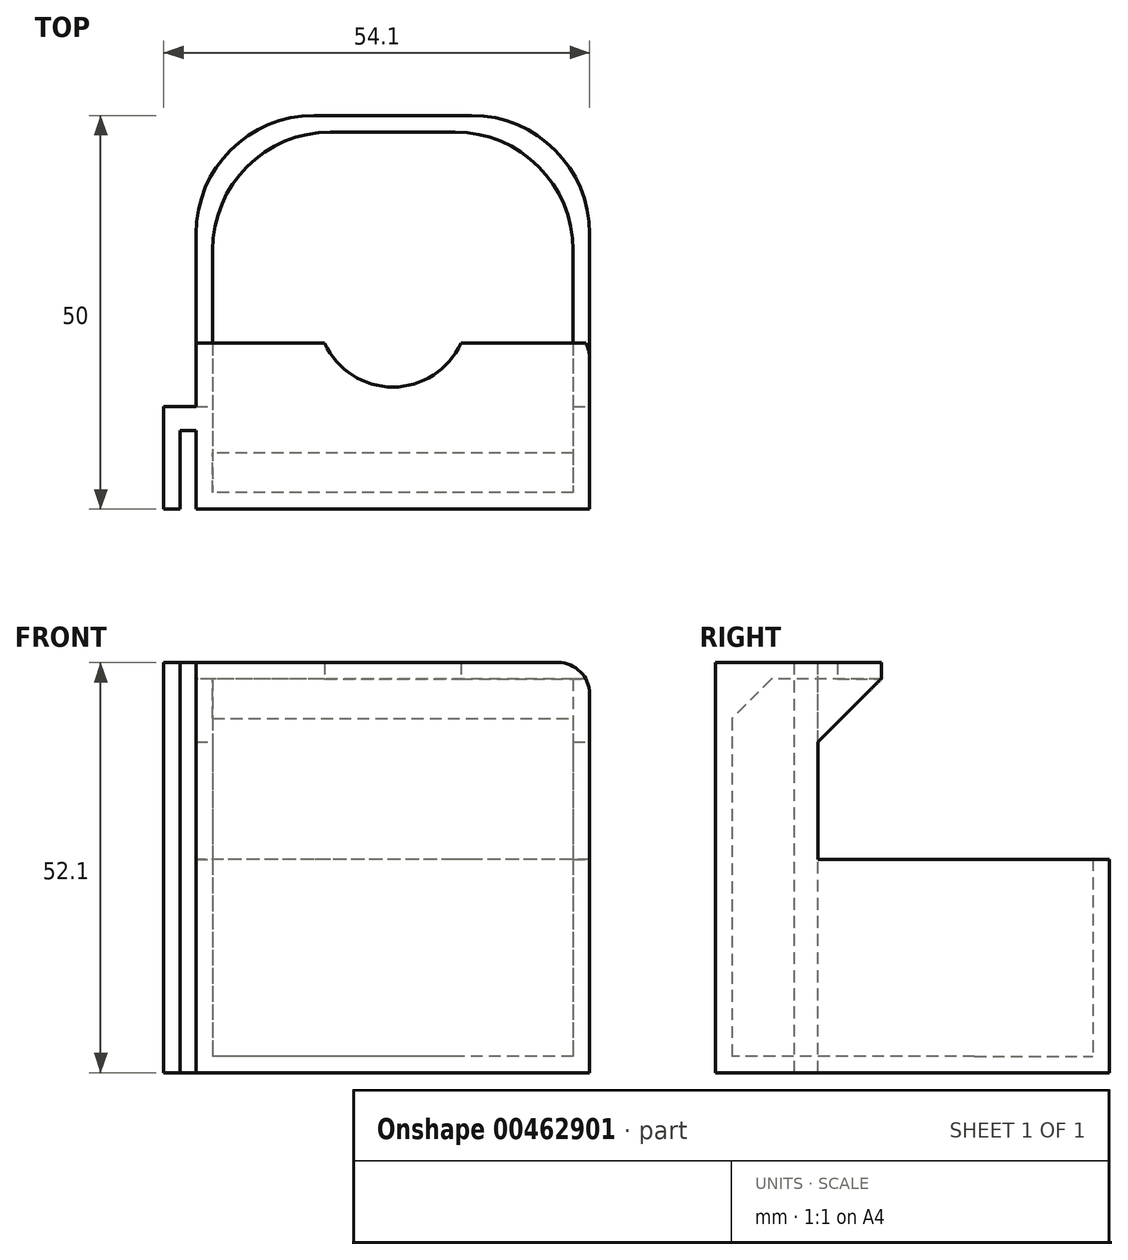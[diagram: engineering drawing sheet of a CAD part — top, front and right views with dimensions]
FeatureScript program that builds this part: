
annotation { "Feature Type Name" : "Feature", "Feature Type Description" : "" }
export const myFeature = defineFeature(function(context is Context, id is Id, definition is map)
    precondition{}
    {
        {
            var Q0;
            Q0=qCreatedBy(makeId("Top.planeOp"),FACE);
            var sketch = newSketch(context, id + "F0", { "sketchPlane" : qUnion([Q0])});
            skLineSegment(sketch, "E0.bottom", {"start": v(25, -25) * mm, "end": v(-25, -25) * mm});
            skLineSegment(sketch, "E0.top", {"start": v(10, 25) * mm, "end": v(-10, 25) * mm});
            skLineSegment(sketch, "E0.left", {"start": v(25, -25) * mm, "end": v(25, 10) * mm});
            skLineSegment(sketch, "E0.right", {"start": v(-25, -25) * mm, "end": v(-25, -15) * mm});
            skPoint(sketch, "E0.middle", {"position": v(0, 0) * mm});
            skLineSegment(sketch, "E1", {"start": v(-25, -25) * mm, "end": v(-27, -25) * mm, "construction": true});
            skLineSegment(sketch, "E2", {"start": v(-27, -25) * mm, "end": v(-27, -15) * mm});
            skLineSegment(sketch, "E3", {"start": v(-27, -25) * mm, "end": v(-29.1, -25) * mm});
            skLineSegment(sketch, "E4", {"start": v(-29.1, -25) * mm, "end": v(-29.1, -12) * mm});
            skLineSegment(sketch, "E5", {"start": v(-29.1, -12) * mm, "end": v(-25, -12) * mm});
            skLineSegment(sketch, "E6", {"start": v(-27, -15) * mm, "end": v(-25, -15) * mm});
            skLineSegment(sketch, "E7.trimOffspring", {"start": v(-25, -12) * mm, "end": v(-25, 10) * mm});
            skLineSegment(sketch, "E8.bottom", {"start": v(7.9, 22.9) * mm, "end": v(-7.9, 22.9) * mm});
            skLineSegment(sketch, "E8.top", {"start": v(22.9, -22.9) * mm, "end": v(-22.9, -22.9) * mm});
            skLineSegment(sketch, "E8.left", {"start": v(22.9, 7.9) * mm, "end": v(22.9, -22.9) * mm});
            skLineSegment(sketch, "E8.right", {"start": v(-22.9, 7.9) * mm, "end": v(-22.9, -22.9) * mm});
            skPoint(sketch, "E9.visualSharp", {"position": v(22.9, 22.9) * mm});
            skArc(sketch, "E9.filletArc", {"start": v(22.9, 7.9) * mm, "mid": v(18.5, 18.5) * mm, "end": v(7.9, 22.9) * mm});
            skPoint(sketch, "E10.visualSharp", {"position": v(-22.9, 22.9) * mm});
            skArc(sketch, "E10.filletArc", {"start": v(-7.9, 22.9) * mm, "mid": v(-18.5, 18.5) * mm, "end": v(-22.9, 7.9) * mm});
            skPoint(sketch, "E11.visualSharp", {"position": v(-25, 25) * mm});
            skArc(sketch, "E11.filletArc", {"start": v(-10, 25) * mm, "mid": v(-20.6, 20.6) * mm, "end": v(-25, 10) * mm});
            skPoint(sketch, "E12.visualSharp", {"position": v(25, 25) * mm});
            skArc(sketch, "E12.filletArc", {"start": v(25, 10) * mm, "mid": v(20.6, 20.6) * mm, "end": v(10, 25) * mm});
            skCircle(sketch, "E13", {"center": v(0, 0) * mm, "radius": 9.5 * mm});
            skLineSegment(sketch, "E14", {"start": v(-8.64, -3.94) * mm, "end": v(-22.9, -3.94) * mm});
            skLineSegment(sketch, "E15", {"start": v(-22.9, -3.94) * mm, "end": v(22.9, -3.94) * mm});
            skLineSegment(sketch, "E16", {"start": v(-22.9, -22.9) * mm, "end": v(-25, -22.9) * mm});
            skLineSegment(sketch, "E17", {"start": v(22.9, -22.9) * mm, "end": v(25, -22.9) * mm});
            skLineSegment(sketch, "E18", {"start": v(-25, -12) * mm, "end": v(-22.9, -12) * mm});
            skLineSegment(sketch, "E19", {"start": v(22.9, -12) * mm, "end": v(25, -12) * mm});
            skLineSegment(sketch, "E20", {"start": v(-25, -3.94) * mm, "end": v(25, -3.94) * mm});
            skSolve(sketch);
        }
        {
            var Q0;
            Q0=makeQuery(id+"F0.imprint","IMPRINT",FACE,{"disambiguationData":[TD([[makeQuery(id+"F0.imprint","IMPRINT",EDGE,{"derivedFrom":sQuery(id+"F0.wireOp",EDGE,"E8.bottom")}),1.0]])]});
            var Q1;
            {var subQ1=sQuery(id+"F0.wireOp",EDGE,"E8.top");Q1=makeQuery(id+"F0.imprint","IMPRINT",FACE,{"disambiguationData":[TD([[makeQuery(id+"F0.imprint","IMPRINT",EDGE,{"derivedFrom":subQ1}),-1.0]])]});}
            var Q2;
            {var subQ0=sQuery(id+"F0.wireOp",EDGE,"E15");var subQ1=sQuery(id+"F0.wireOp",EDGE,"E13");var subQ2=makeQuery(id+"F0.imprint","INTERSECT",VERTEX,{"disambiguationData":[OD(0.0)],"derivedFrom":[subQ1,subQ0]});Q2=makeQuery(id+"F0.imprint","IMPRINT",FACE,{"disambiguationData":[TD([[makeQuery(id+"F0.imprint","IMPRINT",EDGE,{"disambiguationData":[TD([[subQ2,1.0]])],"derivedFrom":subQ1}),1.0]])]});}
            var Q3;
            Q3=makeQuery(id+"F0.imprint","IMPRINT",FACE,{"disambiguationData":[TD([[makeQuery(id+"F0.imprint","IMPRINT",EDGE,{"derivedFrom":sQuery(id+"F0.wireOp",EDGE,"E0.top")}),1.0]])]});
            var Q4;
            {var subQ0=sQuery(id+"F0.wireOp",EDGE,"E15");var subQ1=sQuery(id+"F0.wireOp",EDGE,"E13");var subQ2=makeQuery(id+"F0.imprint","INTERSECT",VERTEX,{"disambiguationData":[OD(0.0)],"derivedFrom":[subQ1,subQ0]});Q4=makeQuery(id+"F0.imprint","IMPRINT",FACE,{"disambiguationData":[TD([[makeQuery(id+"F0.imprint","IMPRINT",EDGE,{"disambiguationData":[TD([[subQ2,-1.0]])],"derivedFrom":subQ1}),1.0]])]});}
            var Q5;
            Q5=makeQuery(id+"F0.imprint","IMPRINT",FACE,{"disambiguationData":[TD([[makeQuery(id+"F0.imprint","IMPRINT",EDGE,{"derivedFrom":sQuery(id+"F0.wireOp",EDGE,"E2")}),1.0]])]});
            var Q6;
            {var subQ1=sQuery(id+"F0.wireOp",EDGE,"E0.bottom");Q6=makeQuery(id+"F0.imprint","IMPRINT",FACE,{"disambiguationData":[TD([[makeQuery(id+"F0.imprint","IMPRINT",EDGE,{"derivedFrom":subQ1}),-1.0]])]});}
            var Q7;
            {var subQ0=sQuery(id+"F0.wireOp",EDGE,"E18");Q7=makeQuery(id+"F0.imprint","IMPRINT",FACE,{"disambiguationData":[TD([[makeQuery(id+"F0.imprint","IMPRINT",EDGE,{"derivedFrom":subQ0}),1.0]])]});}
            var Q8;
            {var subQ0=sQuery(id+"F0.wireOp",EDGE,"E19");Q8=makeQuery(id+"F0.imprint","IMPRINT",FACE,{"disambiguationData":[TD([[makeQuery(id+"F0.imprint","IMPRINT",EDGE,{"derivedFrom":subQ0}),1.0]])]});}
            var Q9;
            {var subQ0=sQuery(id+"F0.wireOp",EDGE,"E17");Q9=makeQuery(id+"F0.imprint","IMPRINT",FACE,{"disambiguationData":[TD([[makeQuery(id+"F0.imprint","IMPRINT",EDGE,{"derivedFrom":subQ0}),1.0]])]});}
            extrude(context, id + "F1", {"entities" : qUnion([Q0, Q1, Q2, Q3, Q4, Q5, Q6, Q7, Q8, Q9]), "oppositeDirection" : true, "depth" : 2.1 * mm});
        }
        {
            var Q0;
            {var subQ5=sQuery(id+"F0.wireOp",EDGE,"E8.top");Q0=makeQuery(id+"F0.imprint","IMPRINT",FACE,{"disambiguationData":[TD([[makeQuery(id+"F0.imprint","IMPRINT",EDGE,{"derivedFrom":subQ5}),-1.0]])]});}
            var Q1;
            Q1=makeQuery(id+"F0.imprint","IMPRINT",FACE,{"disambiguationData":[TD([[makeQuery(id+"F0.imprint","IMPRINT",EDGE,{"derivedFrom":sQuery(id+"F0.wireOp",EDGE,"E2")}),1.0]])]});
            var Q2;
            {var subQ1=sQuery(id+"F0.wireOp",EDGE,"E0.bottom");Q2=makeQuery(id+"F0.imprint","IMPRINT",FACE,{"disambiguationData":[TD([[makeQuery(id+"F0.imprint","IMPRINT",EDGE,{"derivedFrom":subQ1}),-1.0]])]});}
            var Q3;
            {var subQ0=sQuery(id+"F0.wireOp",EDGE,"E17");Q3=makeQuery(id+"F0.imprint","IMPRINT",FACE,{"disambiguationData":[TD([[makeQuery(id+"F0.imprint","IMPRINT",EDGE,{"derivedFrom":subQ0}),1.0]])]});}
            var Q4;
            {var subQ0=sQuery(id+"F0.wireOp",EDGE,"E18");Q4=makeQuery(id+"F0.imprint","IMPRINT",FACE,{"disambiguationData":[TD([[makeQuery(id+"F0.imprint","IMPRINT",EDGE,{"derivedFrom":subQ0}),1.0]])]});}
            var Q5;
            {var subQ0=sQuery(id+"F0.wireOp",EDGE,"E19");Q5=makeQuery(id+"F0.imprint","IMPRINT",FACE,{"disambiguationData":[TD([[makeQuery(id+"F0.imprint","IMPRINT",EDGE,{"derivedFrom":subQ0}),1.0]])]});}
            extrude(context, id + "F2", {"entities" : qUnion([Q0, Q1, Q2, Q3, Q4, Q5]), "operationType" : NewBodyOperationType.ADD, "depth" : 50 * mm, "hasSecondDirection" : true, "secondDirectionOppositeDirection" : true, "secondDirectionDepth" : 2.1 * mm});
        }
        {
            var Q0;
            {var subQ5=sQuery(id+"F0.wireOp",EDGE,"E8.top");Q0=makeQuery(id+"F0.imprint","IMPRINT",FACE,{"disambiguationData":[TD([[makeQuery(id+"F0.imprint","IMPRINT",EDGE,{"derivedFrom":subQ5}),-1.0]])]});}
            var Q1;
            {var subQ0=sQuery(id+"F0.wireOp",EDGE,"E18");Q1=makeQuery(id+"F0.imprint","IMPRINT",FACE,{"disambiguationData":[TD([[makeQuery(id+"F0.imprint","IMPRINT",EDGE,{"derivedFrom":subQ0}),1.0]])]});}
            var Q2;
            {var subQ0=sQuery(id+"F0.wireOp",EDGE,"E19");Q2=makeQuery(id+"F0.imprint","IMPRINT",FACE,{"disambiguationData":[TD([[makeQuery(id+"F0.imprint","IMPRINT",EDGE,{"derivedFrom":subQ0}),1.0]])]});}
            extrude(context, id + "F3", {"entities" : qUnion([Q0, Q1, Q2]), "operationType" : NewBodyOperationType.REMOVE, "depth" : 47.9 * mm});
        }
        {
            var Q0;
            Q0=makeQuery(id+"F3.boolean.opBoolean","COPY",EDGE,{"derivedFrom":makeQuery(id+"F3.opExtrude","CAP_EDGE",EDGE,{"disambiguationData":[OSD([sQuery(id+"F0.wireOp",EDGE,"E8.top")])],"isStart":false})});
            chamfer(context, id + "F4", {"entities" : qUnion([Q0]), "width" : 5 * mm, "tangentPropagation" : true});
        }
        {
            var Q0;
            Q0=makeQuery(id+"F0.imprint","IMPRINT",FACE,{"disambiguationData":[TD([[makeQuery(id+"F0.imprint","IMPRINT",EDGE,{"derivedFrom":sQuery(id+"F0.wireOp",EDGE,"E0.top")}),1.0]])]});
            var Q1;
            {var subQ0=sQuery(id+"F0.wireOp",EDGE,"E18");Q1=makeQuery(id+"F0.imprint","IMPRINT",FACE,{"disambiguationData":[TD([[makeQuery(id+"F0.imprint","IMPRINT",EDGE,{"derivedFrom":subQ0}),1.0]])]});}
            var Q2;
            {var subQ0=sQuery(id+"F0.wireOp",EDGE,"E19");Q2=makeQuery(id+"F0.imprint","IMPRINT",FACE,{"disambiguationData":[TD([[makeQuery(id+"F0.imprint","IMPRINT",EDGE,{"derivedFrom":subQ0}),1.0]])]});}
            extrude(context, id + "F5", {"entities" : qUnion([Q0, Q1, Q2]), "operationType" : NewBodyOperationType.ADD, "depth" : 25 * mm});
        }
        {
            var Q0;
            Q0=makeQuery(id+"F3.boolean.opBoolean","COPY",EDGE,{"derivedFrom":makeQuery(id+"F3.opExtrude","CAP_EDGE",EDGE,{"disambiguationData":[OSD([sQuery(id+"F0.wireOp",EDGE,"E19")])],"isStart":false})});
            var Q1;
            Q1=makeQuery(id+"F3.boolean.opBoolean","COPY",EDGE,{"derivedFrom":makeQuery(id+"F3.opExtrude","CAP_EDGE",EDGE,{"disambiguationData":[OSD([sQuery(id+"F0.wireOp",EDGE,"E18")])],"isStart":false})});
            chamfer(context, id + "F6", {"entities" : qUnion([Q0, Q1]), "width" : 8 * mm, "tangentPropagation" : true});
        }
        {
            var Q0;
            Q0=makeQuery(id+"F2.opExtrude","CAP_EDGE",EDGE,{"disambiguationData":[OSD([sQuery(id+"F0.wireOp",EDGE,"E0.left")])],"isStart":false});
            fillet(context, id + "F7", {"entities" : qUnion([Q0]), "radius" : 4 * mm, "tangentPropagation" : true, "allowEdgeOverflow" : false});
        }
    });
